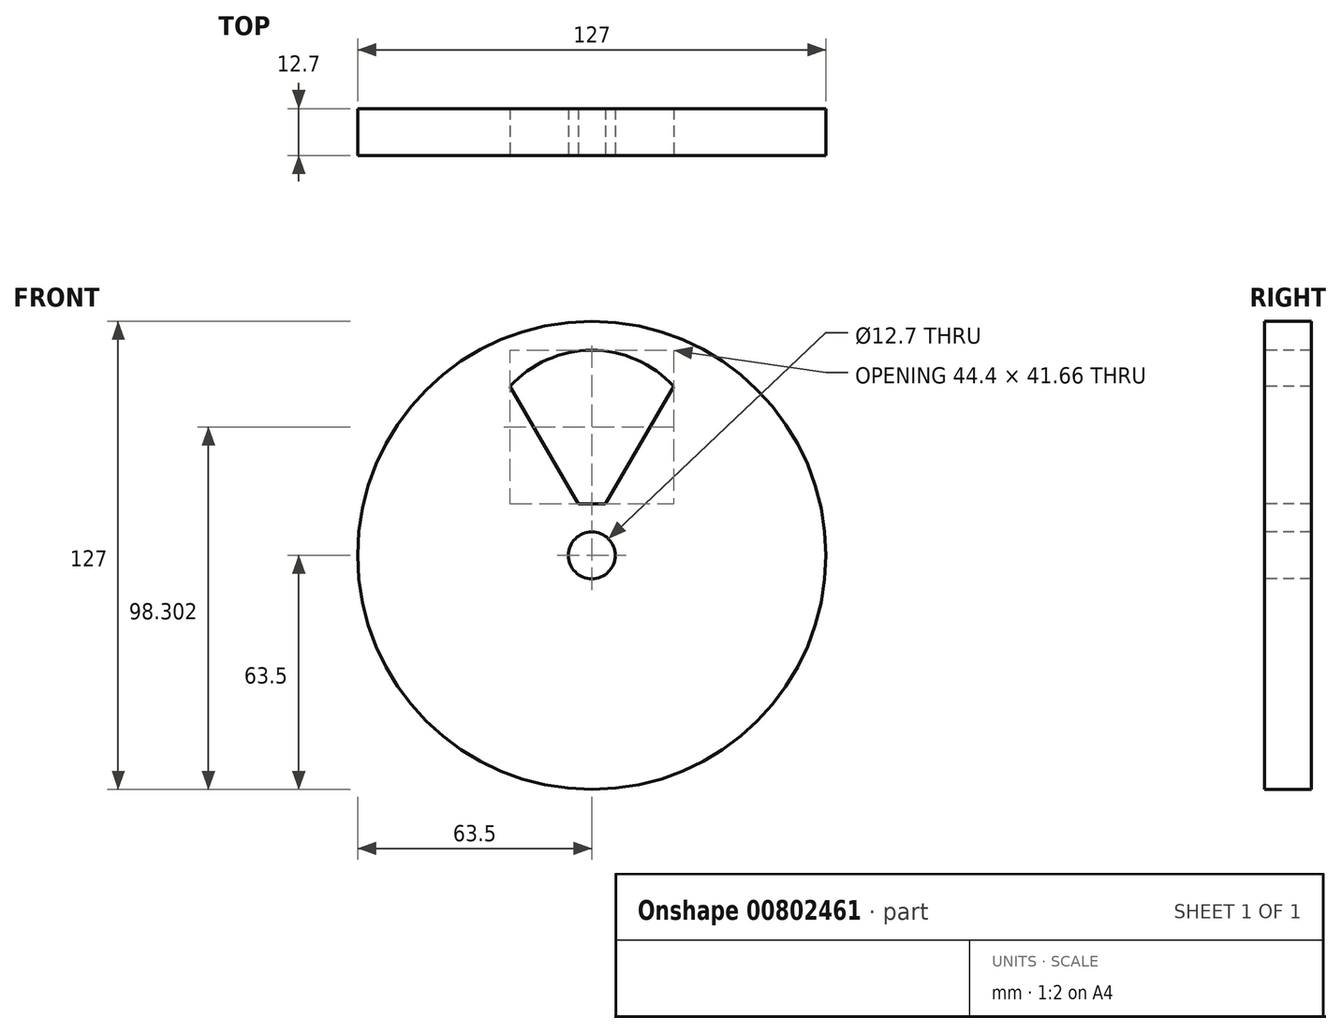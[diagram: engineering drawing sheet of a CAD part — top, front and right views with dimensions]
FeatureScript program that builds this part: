
annotation { "Feature Type Name" : "Feature", "Feature Type Description" : "" }
export const myFeature = defineFeature(function(context is Context, id is Id, definition is map)
    precondition{}
    {
        {
            var Q0;
            Q0=qCreatedBy(makeId("Front.planeOp"),FACE);
            var sketch = newSketch(context, id + "F0", { "sketchPlane" : qUnion([Q0])});
            skCircle(sketch, "E0", {"center": v(0, 0) * mm, "radius": 63.5 * mm});
            skSolve(sketch);
        }
        {
            var Q0;
            Q0 = qSketchRegion(id + "F0", true);
            extrude(context, id + "F1", {"entities" : qUnion([Q0]), "depth" : 12.7 * mm, "offsetDistance" : 25.4 * mm});
        }
        {
            var Q0;
            Q0=makeQuery(id+"F1.opExtrude","CAP_FACE",FACE,{"disambiguationData":[OSD([sQuery(id+"F0.wireOp",EDGE,"E0")])],"isStart":false});
            var sketch = newSketch(context, id + "F2", { "sketchPlane" : qUnion([Q0])});
            skCircle(sketch, "E1", {"center": v(0, 0) * mm, "radius": 6.35 * mm});
            skSolve(sketch);
        }
        {
            var Q0;
            Q0 = qSketchRegion(id + "F2", true);
            extrude(context, id + "F3", {"entities" : qUnion([Q0]), "operationType" : NewBodyOperationType.REMOVE, "endBound" : BoundingType.THROUGH_ALL, "oppositeDirection" : true, "depth" : 25.4 * mm, "offsetDistance" : 25.4 * mm});
        }
        {
            var Q0;
            Q0=makeQuery(id+"F1.opExtrude","CAP_FACE",FACE,{"disambiguationData":[OSD([sQuery(id+"F0.wireOp",EDGE,"E0")])],"isStart":false});
            var sketch = newSketch(context, id + "F4", { "sketchPlane" : qUnion([Q0])});
            skLineSegment(sketch, "E2", {"start": v(-3.71, 13.97) * mm, "end": v(3.71, 13.97) * mm});
            skLineSegment(sketch, "E3", {"start": v(22.2, 45.82) * mm, "end": v(3.71, 13.97) * mm});
            skLineSegment(sketch, "E4", {"start": v(-22.2, 45.82) * mm, "end": v(-3.71, 13.97) * mm});
            skArc(sketch, "E5", {"start": v(22.2, 45.82) * mm, "mid": v(0, 55.63) * mm, "end": v(-22.2, 45.82) * mm});
            skLineSegment(sketch, "E6", {"start": v(0, 0) * mm, "end": v(0, 13.97) * mm, "construction": true});
            skLineSegment(sketch, "E7", {"start": v(0, 13.97) * mm, "end": v(0, 50.81) * mm, "construction": true});
            skSolve(sketch);
        }
        {
            var Q0;
            Q0 = qSketchRegion(id + "F4", true);
            extrude(context, id + "F5", {"entities" : qUnion([Q0]), "operationType" : NewBodyOperationType.REMOVE, "endBound" : BoundingType.THROUGH_ALL, "oppositeDirection" : true, "depth" : 25.4 * mm, "offsetDistance" : 25.4 * mm});
        }
    });
